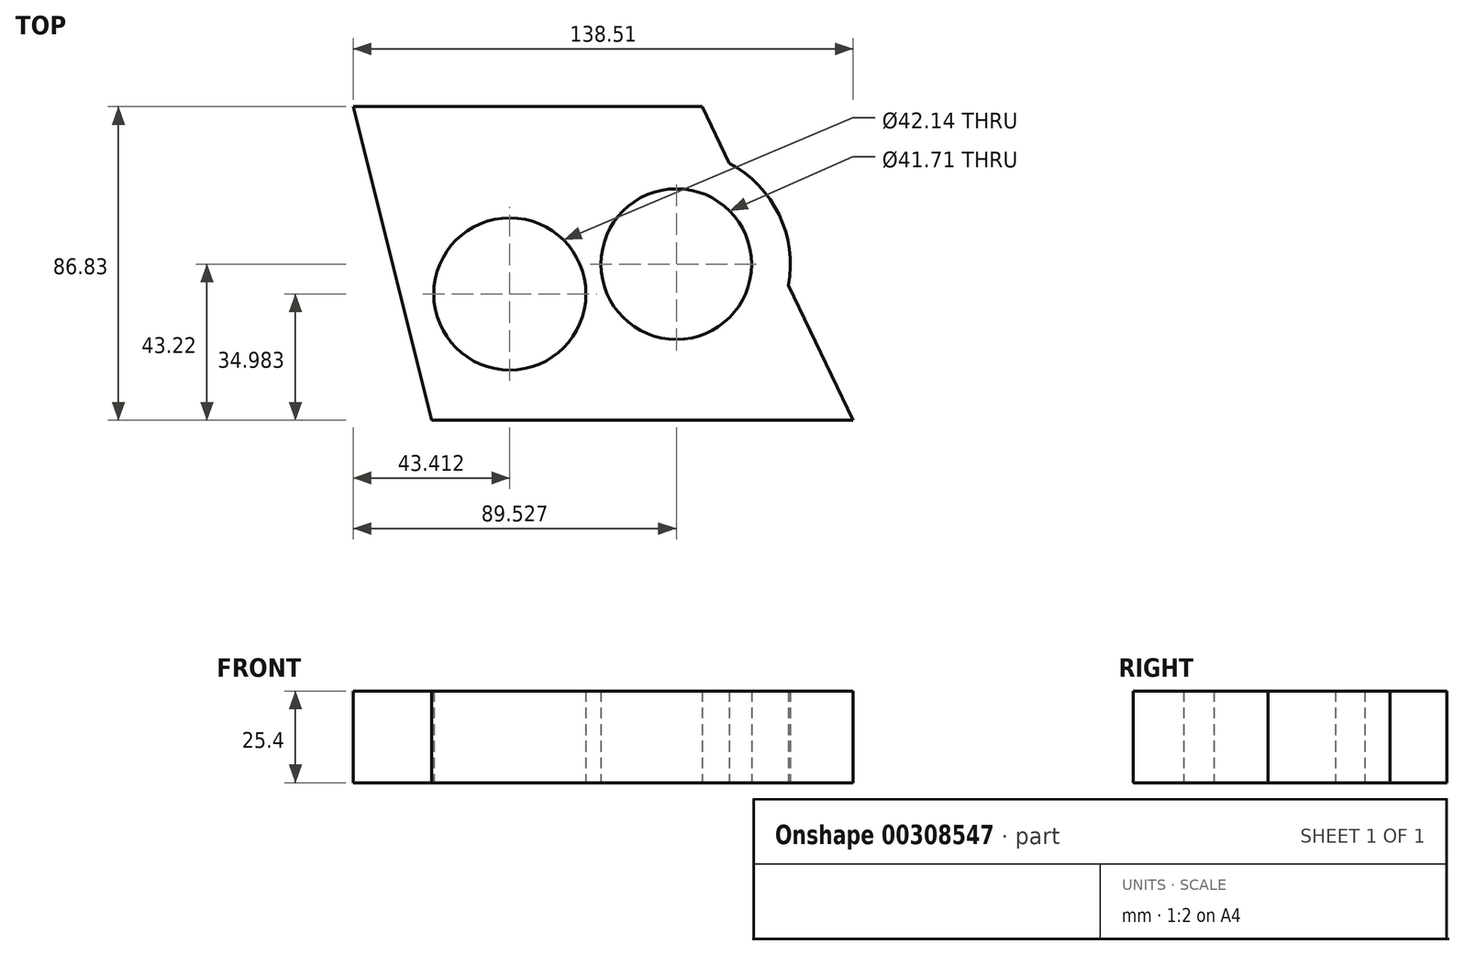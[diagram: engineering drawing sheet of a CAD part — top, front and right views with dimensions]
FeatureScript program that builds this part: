
annotation { "Feature Type Name" : "Feature", "Feature Type Description" : "" }
export const myFeature = defineFeature(function(context is Context, id is Id, definition is map)
    precondition{}
    {
        {
            var Q0;
            Q0=qCreatedBy(makeId("Top.planeOp"),FACE);
            var sketch = newSketch(context, id + "F0", { "sketchPlane" : qUnion([Q0])});
            skLineSegment(sketch, "E0", {"start": v(-138.5, 0) * mm, "end": v(-41.85, 0) * mm});
            skLineSegment(sketch, "E1", {"start": v(-41.85, 0) * mm, "end": v(0, -86.83) * mm});
            skLineSegment(sketch, "E2", {"start": v(0, -86.83) * mm, "end": v(-116.7, -86.83) * mm});
            skLineSegment(sketch, "E3", {"start": v(-116.7, -86.83) * mm, "end": v(-138.5, 0) * mm});
            skCircle(sketch, "E4", {"center": v(-95.1, -51.85) * mm, "radius": 15.97 * mm});
            skCircle(sketch, "E5", {"center": v(-48.98, -43.6) * mm, "radius": 20.86 * mm});
            skCircle(sketch, "E6", {"center": v(-95.1, -51.85) * mm, "radius": 21.07 * mm});
            skCircle(sketch, "E7", {"center": v(-48.98, -43.6) * mm, "radius": 31.56 * mm});
            skSolve(sketch);
        }
        {
            var Q0;
            Q0 = qSketchRegion(id + "F0", true);
            extrude(context, id + "F1", {"entities" : qUnion([Q0]), "depth" : 25.4 * mm});
        }
    });
